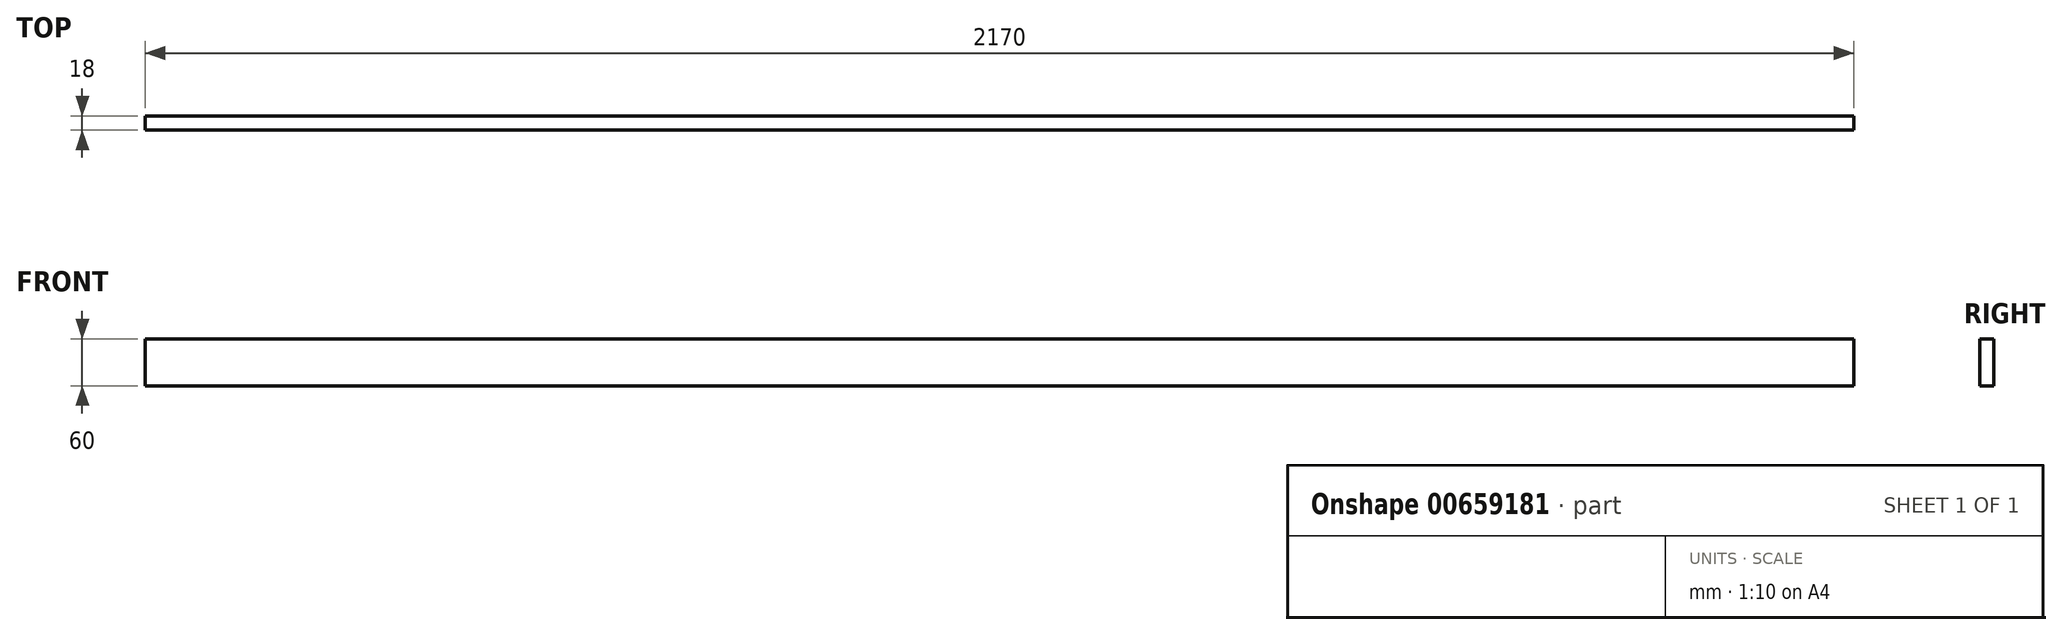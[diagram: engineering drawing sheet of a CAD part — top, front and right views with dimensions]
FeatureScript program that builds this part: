
annotation { "Feature Type Name" : "Feature", "Feature Type Description" : "" }
export const myFeature = defineFeature(function(context is Context, id is Id, definition is map)
    precondition{}
    {
        {
            var Q0;
            Q0=qCreatedBy(makeId("Front.planeOp"),FACE);
            var sketch = newSketch(context, id + "F0", { "sketchPlane" : qUnion([Q0])});
            skLineSegment(sketch, "E0.bottom", {"start": v(1085, -30) * mm, "end": v(-1085, -30) * mm});
            skLineSegment(sketch, "E0.top", {"start": v(1085, 30) * mm, "end": v(-1085, 30) * mm});
            skLineSegment(sketch, "E0.left", {"start": v(1085, -30) * mm, "end": v(1085, 30) * mm});
            skLineSegment(sketch, "E0.right", {"start": v(-1085, -30) * mm, "end": v(-1085, 30) * mm});
            skPoint(sketch, "E0.middle", {"position": v(0, 0) * mm});
            skSolve(sketch);
        }
        {
            var Q0;
            Q0=makeQuery(id+"F0.imprint","IMPRINT",FACE,{"disambiguationData":[TD([[makeQuery(id+"F0.imprint","IMPRINT",EDGE,{"derivedFrom":sQuery(id+"F0.wireOp",EDGE,"E0.bottom")}),-1.0]])]});
            extrude(context, id + "F1", {"entities" : qUnion([Q0]), "endBound" : BoundingType.SYMMETRIC, "depth" : 18 * mm, "offsetDistance" : 25 * mm});
        }
    });
